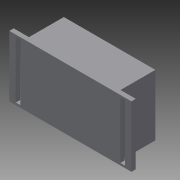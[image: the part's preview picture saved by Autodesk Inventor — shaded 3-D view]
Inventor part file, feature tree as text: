
AUTODESK INVENTOR PART (.ipt)
format: ipt  version: 2013 (Build 170138000, 138)  size: 102,400 bytes
history: native  units: mm
features: sketch x3, extrude x2, hole x1
ambient origin geometry x8: Origin, YZ Plane, XZ Plane, XY Plane, X Axis, Y Axis, Z Axis, Center Point
bodies: Solid1 (feature_tree)
feature tree (6):
  extrude  "Extrusion1"  Depth=88.9mm
  extrude  "Extrusion2"  Depth=82.55mm
  hole  "Hole1"  [1 undecoded]
  sketch  "Sketch1"  dims[d0=177.8mm d1=88.9mm]
  sketch  "Sketch2"  dims[d2=6.7564mm d3=82.55mm]
  sketch  "Sketch3"  dims[d4=6.7564mm d5=82.55mm d6=6.35mm d7=0.0mm d8=133.35mm d9=88.9mm d10=50.8mm d11=0.0mm d12=122.0mm d13=40.0mm d14=2.4638mm d15=19.05mm d16=9.525mm d17=6.35mm d18=14.3117mm d19=12.7mm d20=20.594885mm]
note: 1 required parameter value undecoded (feature->parameter linkage not recoverable at this tier; creation-order binding heuristic only, values carry confidence <= 0.55)
